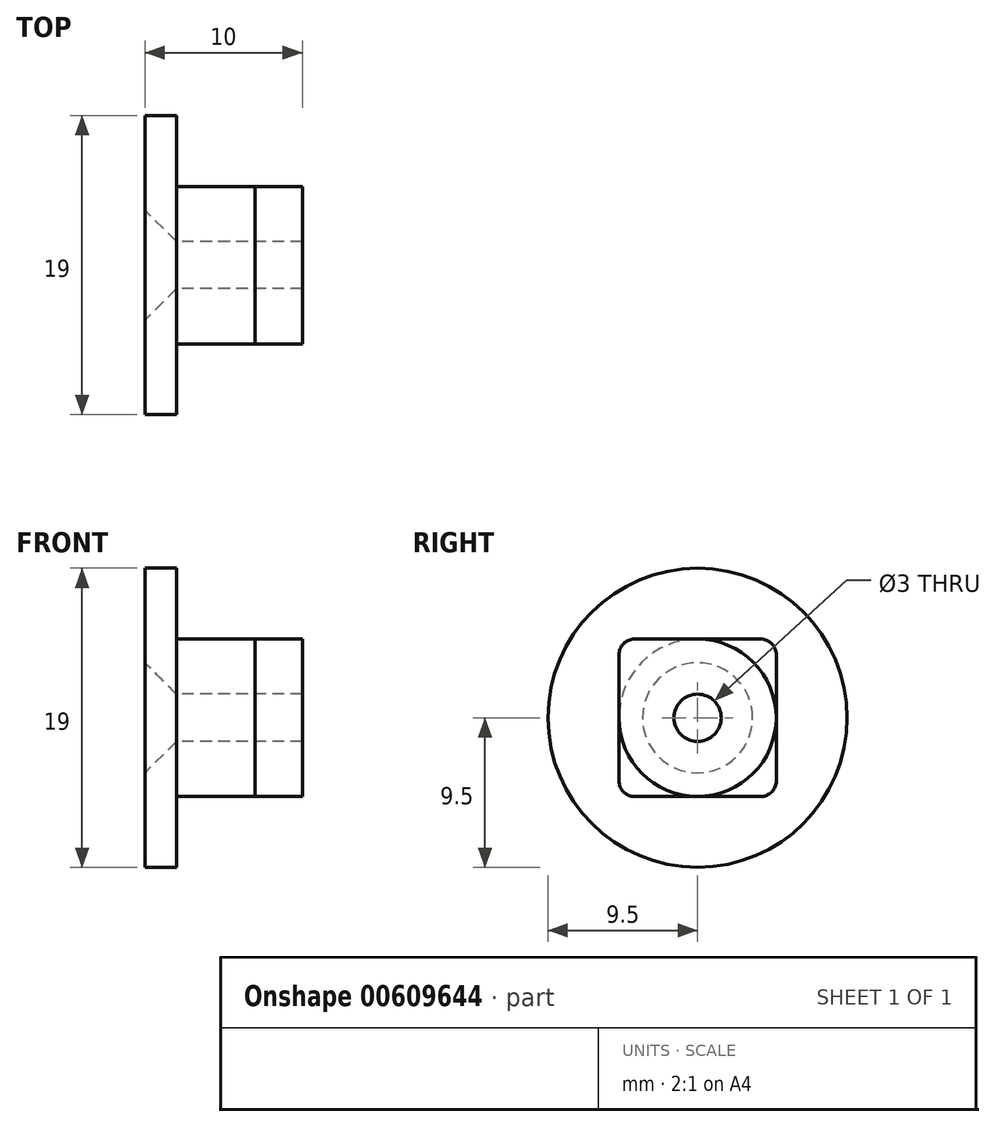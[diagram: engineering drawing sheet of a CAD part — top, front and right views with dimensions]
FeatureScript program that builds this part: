
annotation { "Feature Type Name" : "Feature", "Feature Type Description" : "" }
export const myFeature = defineFeature(function(context is Context, id is Id, definition is map)
    precondition{}
    {
        {
            var Q0;
            Q0=qCreatedBy(makeId("Right.planeOp"),FACE);
            var sketch = newSketch(context, id + "F0", { "sketchPlane" : qUnion([Q0])});
            skCircle(sketch, "E0", {"center": v(0, 0) * mm, "radius": 9.5 * mm});
            skSolve(sketch);
        }
        {
            var Q0;
            Q0 = qSketchRegion(id + "F0", true);
            extrude(context, id + "F1", {"entities" : qUnion([Q0]), "depth" : 2 * mm, "offsetDistance" : 25 * mm});
        }
        {
            var Q0;
            Q0=qCreatedBy(makeId("Right.planeOp"),FACE);
            var sketch = newSketch(context, id + "F2", { "sketchPlane" : qUnion([Q0])});
            skCircle(sketch, "E1", {"center": v(0, 0) * mm, "radius": 5 * mm});
            skSolve(sketch);
        }
        {
            var Q0;
            Q0 = qSketchRegion(id + "F2", true);
            extrude(context, id + "F3", {"entities" : qUnion([Q0]), "operationType" : NewBodyOperationType.ADD, "depth" : 7 * mm, "offsetDistance" : 25 * mm});
        }
        {
            var Q0;
            Q0=qCreatedBy(makeId("Right.planeOp"),FACE);
            var sketch = newSketch(context, id + "F4", { "sketchPlane" : qUnion([Q0])});
            skPoint(sketch, "E2", {"position": v(0, 0) * mm});
            skSolve(sketch);
        }
        {
            var Q0;
            Q0=makeQuery(id+"F3.opExtrude","CAP_FACE",FACE,{"disambiguationData":[OSD([sQuery(id+"F2.wireOp",EDGE,"E1")])],"isStart":false});
            var sketch = newSketch(context, id + "F5", { "sketchPlane" : qUnion([Q0])});
            skLineSegment(sketch, "E3.bottom", {"start": v(-4, 5) * mm, "end": v(4, 5) * mm});
            skLineSegment(sketch, "E3.top", {"start": v(-4, -5) * mm, "end": v(4, -5) * mm});
            skLineSegment(sketch, "E3.left", {"start": v(-5, 4) * mm, "end": v(-5, -4) * mm});
            skLineSegment(sketch, "E3.right", {"start": v(5, 4) * mm, "end": v(5, -4) * mm});
            skPoint(sketch, "E4.visualSharp", {"position": v(-5, 5) * mm});
            skArc(sketch, "E4.filletArc", {"start": v(-4, 5) * mm, "mid": v(-4.7, 4.7) * mm, "end": v(-5, 4) * mm});
            skPoint(sketch, "E5.visualSharp", {"position": v(5, 5) * mm});
            skArc(sketch, "E5.filletArc", {"start": v(5, 4) * mm, "mid": v(4.71, 4.7) * mm, "end": v(4, 5) * mm});
            skPoint(sketch, "E6.visualSharp", {"position": v(5, -5) * mm});
            skArc(sketch, "E6.filletArc", {"start": v(4, -5) * mm, "mid": v(4.71, -4.71) * mm, "end": v(5, -4) * mm});
            skPoint(sketch, "E7.visualSharp", {"position": v(-5, -5) * mm});
            skArc(sketch, "E7.filletArc", {"start": v(-5, -4) * mm, "mid": v(-4.7, -4.71) * mm, "end": v(-4, -5) * mm});
            skSolve(sketch);
        }
        {
            var Q0;
            Q0 = qSketchRegion(id + "F5", true);
            extrude(context, id + "F6", {"entities" : qUnion([Q0]), "operationType" : NewBodyOperationType.ADD, "depth" : 3 * mm, "hasOffset" : true, "offsetDistance" : 3 * mm});
        }
        {
            var Q0;
            Q0=sQuery(id+"F4.wireOp",VERTEX,"E2");
            var Q1;
            Q1=makeQuery(id+"F1.opExtrude","SWEPT_BODY",BODY,{"disambiguationData":[OSD([sQuery(id+"F0.wireOp",EDGE,"E0")])]});
            hole(context, id + "F7", {"style" : HoleStyle.C_SINK, "endStyle" : HoleEndStyle.THROUGH, "oppositeDirection" : true, "holeDiameter" : 3 * mm, "cSinkDiameter" : 7 * mm, "cSinkAngle" : 90 * degree, "majorDiameter" : 5 * mm, "isTappedThrough" : true, "tappedDepth" : 12 * mm, "tapClearance" : 3, "startFromSketch" : true, "locations" : qUnion([Q0]), "scope" : qUnion([Q1])});
        }
    });
